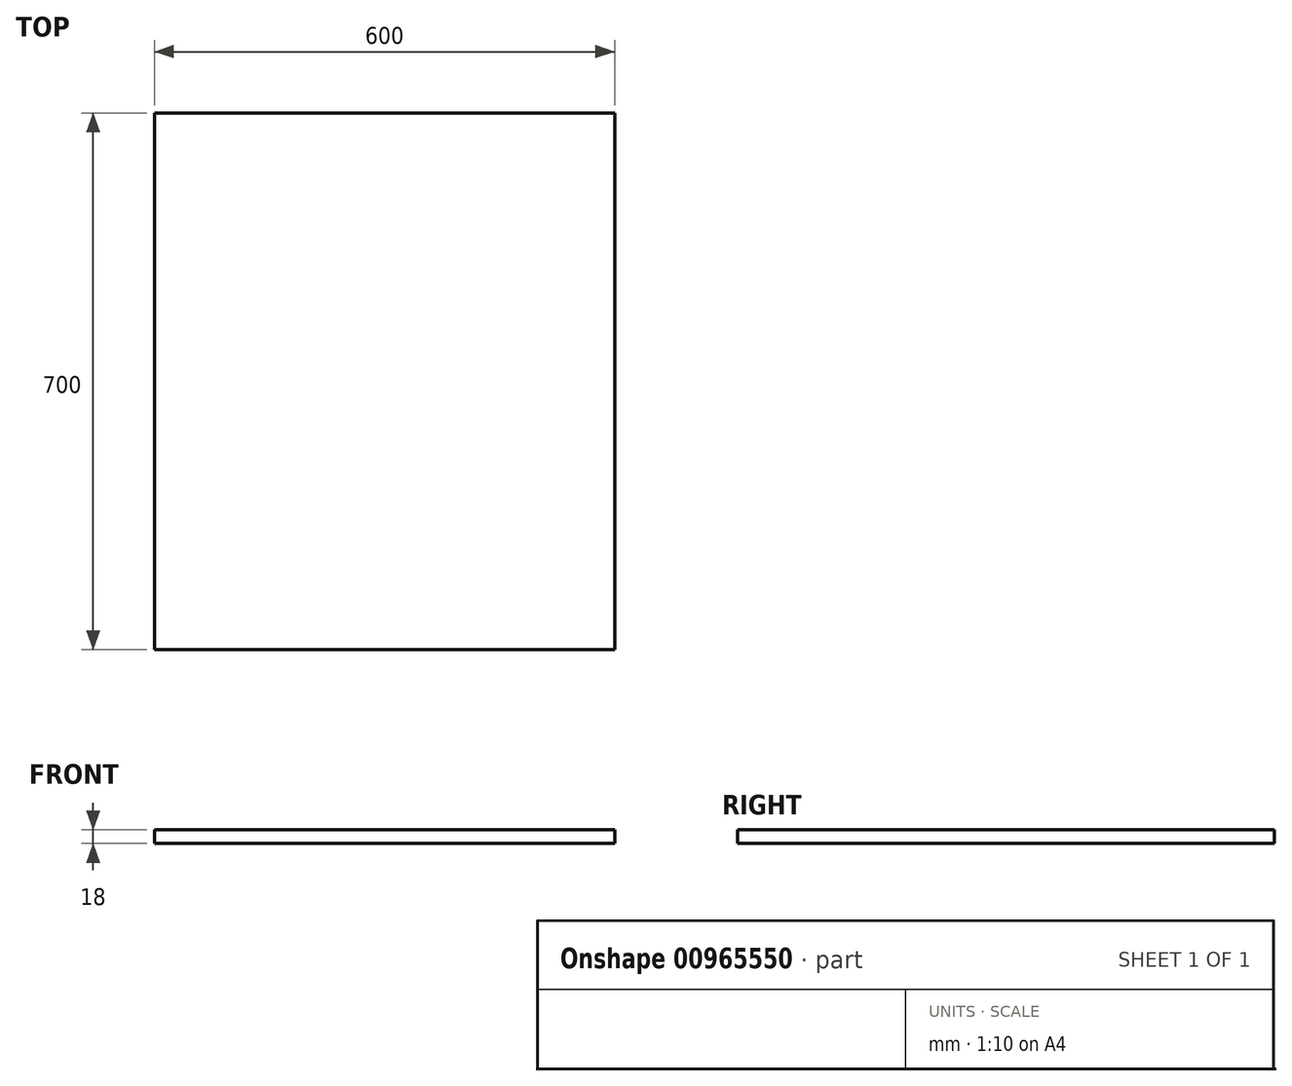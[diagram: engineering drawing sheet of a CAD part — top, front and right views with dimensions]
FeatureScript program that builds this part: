
annotation { "Feature Type Name" : "Feature", "Feature Type Description" : "" }
export const myFeature = defineFeature(function(context is Context, id is Id, definition is map)
    precondition{}
    {
        {
            var Q0;
            Q0=qCreatedBy(makeId("Top.planeOp"),FACE);
            var sketch = newSketch(context, id + "F0", { "sketchPlane" : qUnion([Q0])});
            skLineSegment(sketch, "E0.bottom", {"start": v(300, 350) * mm, "end": v(-300, 350) * mm});
            skLineSegment(sketch, "E0.top", {"start": v(300, -350) * mm, "end": v(-300, -350) * mm});
            skLineSegment(sketch, "E0.left", {"start": v(300, 350) * mm, "end": v(300, -350) * mm});
            skLineSegment(sketch, "E0.right", {"start": v(-300, 350) * mm, "end": v(-300, -350) * mm});
            skPoint(sketch, "E0.middle", {"position": v(0, 0) * mm});
            skSolve(sketch);
        }
        {
            var Q0;
            Q0=makeQuery(id+"F0.imprint","IMPRINT",FACE,{"disambiguationData":[TD([[makeQuery(id+"F0.imprint","IMPRINT",EDGE,{"derivedFrom":sQuery(id+"F0.wireOp",EDGE,"E0.bottom")}),1.0]])]});
            extrude(context, id + "F1", {"entities" : qUnion([Q0]), "depth" : 18 * mm, "offsetDistance" : 25 * mm});
        }
    });
